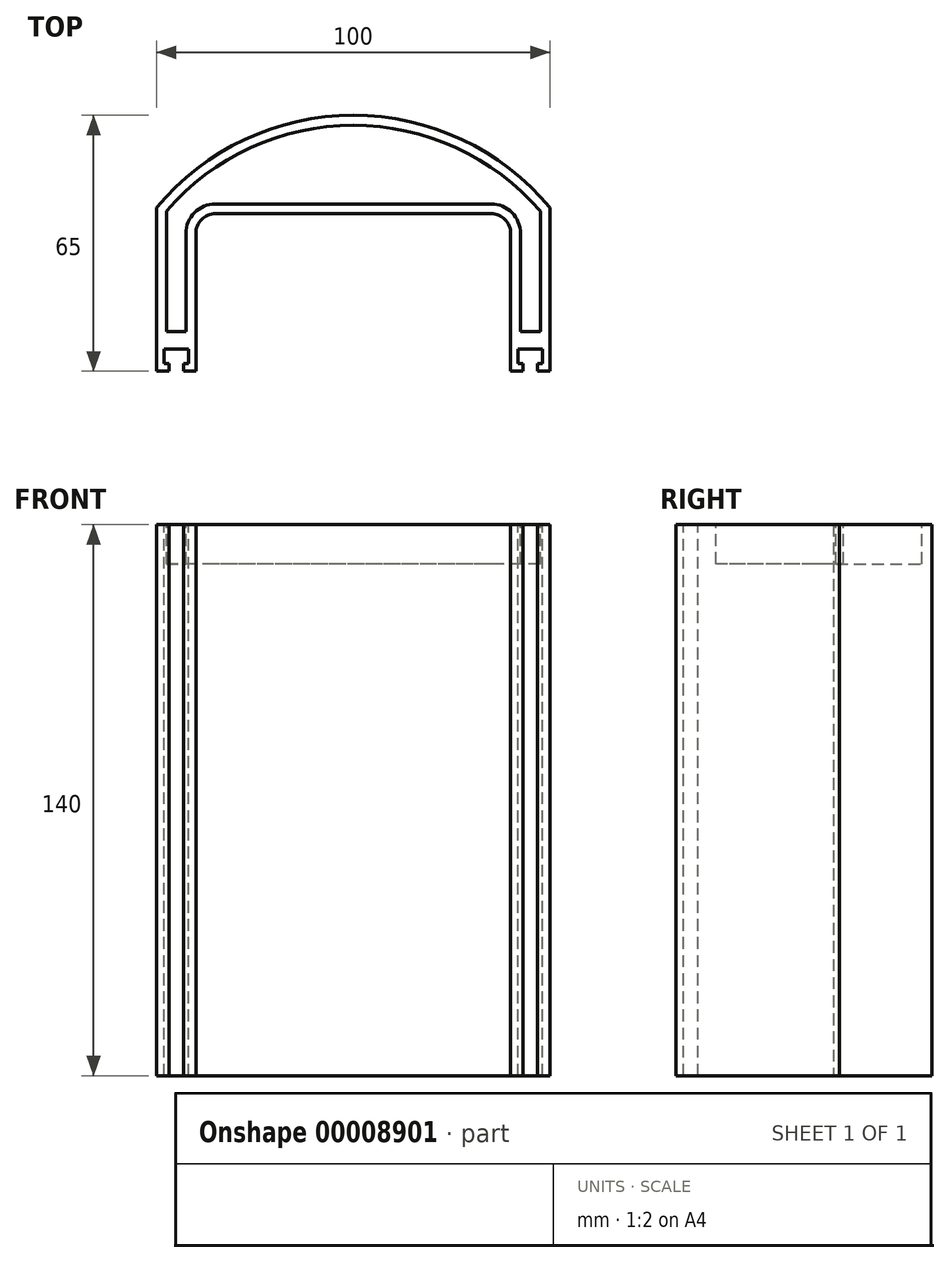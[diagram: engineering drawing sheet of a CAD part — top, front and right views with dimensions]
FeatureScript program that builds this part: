
annotation { "Feature Type Name" : "Feature", "Feature Type Description" : "" }
export const myFeature = defineFeature(function(context is Context, id is Id, definition is map)
    precondition{}
    {
        {
            var Q0;
            Q0=qCreatedBy(makeId("Top.planeOp"),FACE);
            var sketch = newSketch(context, id + "F0", { "sketchPlane" : qUnion([Q0])});
            skLineSegment(sketch, "E0", {"start": v(0, 0) * mm, "end": v(-40, 0) * mm});
            skLineSegment(sketch, "E1", {"start": v(0, 0) * mm, "end": v(40, 0) * mm});
            skLineSegment(sketch, "E2", {"start": v(0, 35) * mm, "end": v(0, 0) * mm});
            skLineSegment(sketch, "E3", {"start": v(-40, 0) * mm, "end": v(-43.59, 0) * mm});
            skLineSegment(sketch, "E4", {"start": v(40, 0) * mm, "end": v(43.59, 0) * mm});
            skLineSegment(sketch, "E5", {"start": v(-43.59, 0) * mm, "end": v(-50, 0) * mm});
            skLineSegment(sketch, "E6", {"start": v(43.59, 0) * mm, "end": v(50, 0) * mm});
            skCircle(sketch, "E7.0", {"center": v(0, 0) * mm, "radius": 65 * mm});
            skLineSegment(sketch, "E8.0", {"start": v(40, 35) * mm, "end": v(40, 0) * mm});
            skLineSegment(sketch, "E9.0", {"start": v(-40, 35) * mm, "end": v(-40, 0) * mm});
            skLineSegment(sketch, "E10.0", {"start": v(0, 40) * mm, "end": v(-35, 40) * mm});
            skLineSegment(sketch, "E10.1", {"start": v(0, 40) * mm, "end": v(35, 40) * mm});
            skPoint(sketch, "E11.visualSharp", {"position": v(-40, 40) * mm});
            skArc(sketch, "E11.filletArc", {"start": v(-35, 40) * mm, "mid": v(-38.54, 38.54) * mm, "end": v(-40, 35) * mm});
            skPoint(sketch, "E12.visualSharp", {"position": v(40, 40) * mm});
            skArc(sketch, "E12.filletArc", {"start": v(40, 35) * mm, "mid": v(38.54, 38.54) * mm, "end": v(35, 40) * mm});
            skLineSegment(sketch, "E13.0", {"start": v(-50, 41.53) * mm, "end": v(-50, 0) * mm});
            skLineSegment(sketch, "E14.0", {"start": v(50, 41.53) * mm, "end": v(50, 0) * mm});
            skSolve(sketch);
        }
        {
            var Q0;
            Q0=makeQuery(id+"F0.imprint","IMPRINT",FACE,{"disambiguationData":[TD([[makeQuery(id+"F0.imprint","IMPRINT",EDGE,{"derivedFrom":sQuery(id+"F0.wireOp",EDGE,"E3")}),-1.0]])]});
            extrude(context, id + "F1", {"entities" : qUnion([Q0]), "depth" : 190 * mm});
        }
        {
            var Q0;
            Q0=makeQuery(id+"F1.opExtrude","CAP_FACE",FACE,{"disambiguationData":[OSD([sQuery(id+"F0.wireOp",EDGE,"E3"),sQuery(id+"F0.wireOp",EDGE,"E4"),sQuery(id+"F0.wireOp",EDGE,"E5"),sQuery(id+"F0.wireOp",EDGE,"E6"),sQuery(id+"F0.wireOp",EDGE,"E7.0"),sQuery(id+"F0.wireOp",EDGE,"E8.0"),sQuery(id+"F0.wireOp",EDGE,"E9.0"),sQuery(id+"F0.wireOp",EDGE,"E10.0"),sQuery(id+"F0.wireOp",EDGE,"E10.1"),sQuery(id+"F0.wireOp",EDGE,"E11.filletArc"),sQuery(id+"F0.wireOp",EDGE,"E12.filletArc"),sQuery(id+"F0.wireOp",EDGE,"E13.0"),sQuery(id+"F0.wireOp",EDGE,"E14.0")])],"isStart":false});
            var sketch = newSketch(context, id + "F2", { "sketchPlane" : qUnion([Q0])});
            skLineSegment(sketch, "E15.0", {"start": v(35, 32.9) * mm, "end": v(35, 0) * mm});
            skLineSegment(sketch, "E16", {"start": v(-50, 0) * mm, "end": v(-50, 5) * mm});
            skLineSegment(sketch, "E17.0", {"start": v(-43.75, 0) * mm, "end": v(-43.75, 2.5) * mm, "construction": true});
            skLineSegment(sketch, "E18.0", {"start": v(-46.25, 0) * mm, "end": v(-46.25, 2.5) * mm, "construction": true});
            skLineSegment(sketch, "E19.0", {"start": v(-47.5, 2.5) * mm, "end": v(-47.5, 5) * mm, "construction": true});
            skLineSegment(sketch, "E20.0", {"start": v(-42.5, 2.5) * mm, "end": v(-42.5, 5) * mm, "construction": true});
            skLineSegment(sketch, "E21", {"start": v(-47.5, 5) * mm, "end": v(-42.5, 5) * mm, "construction": true});
            skLineSegment(sketch, "E22.0", {"start": v(-47.5, 2.5) * mm, "end": v(-46.25, 2.5) * mm, "construction": true});
            skLineSegment(sketch, "E23.trimOffspring", {"start": v(-43.75, 2.5) * mm, "end": v(-42.5, 2.5) * mm, "construction": true});
            skLineSegment(sketch, "E24.0", {"start": v(-48.1, 1.9) * mm, "end": v(-48.1, 5.6) * mm});
            skLineSegment(sketch, "E25.0", {"start": v(-48.1, 5.6) * mm, "end": v(-41.9, 5.6) * mm});
            skLineSegment(sketch, "E26.0", {"start": v(-41.9, 1.9) * mm, "end": v(-41.9, 5.6) * mm});
            skLineSegment(sketch, "E27.0", {"start": v(-48.1, 1.9) * mm, "end": v(-46.85, 1.9) * mm});
            skLineSegment(sketch, "E28.0", {"start": v(-43.15, 1.9) * mm, "end": v(-41.9, 1.9) * mm});
            skLineSegment(sketch, "E29.0", {"start": v(-46.85, 0) * mm, "end": v(-46.85, 1.9) * mm});
            skLineSegment(sketch, "E30.0", {"start": v(-43.15, 0) * mm, "end": v(-43.15, 1.9) * mm});
            skLineSegment(sketch, "E31", {"start": v(50, 0) * mm, "end": v(50, 5) * mm});
            skLineSegment(sketch, "E32.0", {"start": v(46.25, 0) * mm, "end": v(46.25, 2.5) * mm, "construction": true});
            skLineSegment(sketch, "E33.0", {"start": v(47.5, 2.5) * mm, "end": v(47.5, 5) * mm, "construction": true});
            skLineSegment(sketch, "E34.0", {"start": v(43.75, 0) * mm, "end": v(43.75, 2.5) * mm, "construction": true});
            skLineSegment(sketch, "E35.0", {"start": v(42.5, 2.5) * mm, "end": v(42.5, 5) * mm, "construction": true});
            skLineSegment(sketch, "E36", {"start": v(47.5, 5) * mm, "end": v(42.5, 5) * mm, "construction": true});
            skLineSegment(sketch, "E37.0", {"start": v(47.5, 2.5) * mm, "end": v(46.25, 2.5) * mm, "construction": true});
            skLineSegment(sketch, "E38.trimOffspring", {"start": v(43.75, 2.5) * mm, "end": v(42.5, 2.5) * mm, "construction": true});
            skLineSegment(sketch, "E39.0", {"start": v(48.1, 5.6) * mm, "end": v(41.9, 5.6) * mm});
            skLineSegment(sketch, "E40.0", {"start": v(48.1, 1.9) * mm, "end": v(48.1, 5.6) * mm});
            skLineSegment(sketch, "E41.0", {"start": v(41.9, 1.9) * mm, "end": v(41.9, 5.6) * mm});
            skLineSegment(sketch, "E42.0", {"start": v(43.15, 0) * mm, "end": v(43.15, 1.9) * mm});
            skLineSegment(sketch, "E43.0", {"start": v(46.85, 0) * mm, "end": v(46.85, 1.9) * mm});
            skLineSegment(sketch, "E44.0", {"start": v(48.1, 1.9) * mm, "end": v(46.85, 1.9) * mm});
            skLineSegment(sketch, "E45.0", {"start": v(43.15, 1.9) * mm, "end": v(41.9, 1.9) * mm});
            skSolve(sketch);
        }
        {
            var Q0;
            Q0=makeQuery(id+"F2.imprint","IMPRINT",FACE,{"disambiguationData":[TD([[makeQuery(id+"F2.imprint","IMPRINT",EDGE,{"derivedFrom":sQuery(id+"F2.wireOp",EDGE,"E39.0")}),1.0]])]});
            var Q1;
            Q1=makeQuery(id+"F2.imprint","IMPRINT",FACE,{"disambiguationData":[TD([[makeQuery(id+"F2.imprint","IMPRINT",EDGE,{"derivedFrom":sQuery(id+"F2.wireOp",EDGE,"E24.0")}),-1.0]])]});
            extrude(context, id + "F3", {"entities" : qUnion([Q0, Q1]), "operationType" : NewBodyOperationType.REMOVE, "oppositeDirection" : true, "depth" : 190 * mm});
        }
        {
            var Q0;
            Q0=makeQuery(id+"F1.opExtrude","CAP_FACE",FACE,{"disambiguationData":[OSD([sQuery(id+"F0.wireOp",EDGE,"E3"),sQuery(id+"F0.wireOp",EDGE,"E4"),sQuery(id+"F0.wireOp",EDGE,"E5"),sQuery(id+"F0.wireOp",EDGE,"E6"),sQuery(id+"F0.wireOp",EDGE,"E7.0"),sQuery(id+"F0.wireOp",EDGE,"E8.0"),sQuery(id+"F0.wireOp",EDGE,"E9.0"),sQuery(id+"F0.wireOp",EDGE,"E10.0"),sQuery(id+"F0.wireOp",EDGE,"E10.1"),sQuery(id+"F0.wireOp",EDGE,"E11.filletArc"),sQuery(id+"F0.wireOp",EDGE,"E12.filletArc"),sQuery(id+"F0.wireOp",EDGE,"E13.0"),sQuery(id+"F0.wireOp",EDGE,"E14.0")])],"isStart":false});
            extrude(context, id + "F4", {"entities" : qUnion([Q0]), "operationType" : NewBodyOperationType.REMOVE, "oppositeDirection" : true, "depth" : 50 * mm});
        }
        {
            var Q0;
            Q0=makeQuery(id+"F4.boolean.opBoolean","COPY",FACE,{"derivedFrom":makeQuery(id+"F4.opExtrude","CAP_FACE",FACE,{"disambiguationData":[OSD([sQuery(id+"F0.wireOp",EDGE,"E3"),sQuery(id+"F0.wireOp",EDGE,"E4"),sQuery(id+"F0.wireOp",EDGE,"E5"),sQuery(id+"F0.wireOp",EDGE,"E6"),sQuery(id+"F0.wireOp",EDGE,"E7.0"),sQuery(id+"F0.wireOp",EDGE,"E8.0"),sQuery(id+"F0.wireOp",EDGE,"E9.0"),sQuery(id+"F0.wireOp",EDGE,"E10.0"),sQuery(id+"F0.wireOp",EDGE,"E10.1"),sQuery(id+"F0.wireOp",EDGE,"E11.filletArc"),sQuery(id+"F0.wireOp",EDGE,"E12.filletArc"),sQuery(id+"F0.wireOp",EDGE,"E13.0"),sQuery(id+"F0.wireOp",EDGE,"E14.0")])],"isStart":false})});
            var sketch = newSketch(context, id + "F5", { "sketchPlane" : qUnion([Q0])});
            skLineSegment(sketch, "E46.0", {"start": v(-48.1, 10.6) * mm, "end": v(-41.9, 10.6) * mm, "construction": true});
            skLineSegment(sketch, "E47.0", {"start": v(48.1, 10.6) * mm, "end": v(41.9, 10.6) * mm, "construction": true});
            skLineSegment(sketch, "E48.0", {"start": v(-47.5, 40.62) * mm, "end": v(-47.5, 0) * mm});
            skArc(sketch, "E48.1", {"start": v(47.5, 40.62) * mm, "mid": v(0, 62.5) * mm, "end": v(-47.5, 40.62) * mm});
            skLineSegment(sketch, "E48.2", {"start": v(47.5, 40.62) * mm, "end": v(47.5, 0) * mm});
            skLineSegment(sketch, "E49.0", {"start": v(-42.5, 35) * mm, "end": v(-42.5, 0) * mm});
            skArc(sketch, "E49.1", {"start": v(-35, 42.5) * mm, "mid": v(-40.3, 40.3) * mm, "end": v(-42.5, 35) * mm});
            skLineSegment(sketch, "E49.2", {"start": v(35, 42.5) * mm, "end": v(-35, 42.5) * mm});
            skArc(sketch, "E49.3", {"start": v(42.5, 35) * mm, "mid": v(40.3, 40.3) * mm, "end": v(35, 42.5) * mm});
            skLineSegment(sketch, "E49.4", {"start": v(42.5, 35) * mm, "end": v(42.5, 0) * mm});
            skLineSegment(sketch, "E50.0", {"start": v(-48.1, 10.1) * mm, "end": v(-41.9, 10.1) * mm});
            skLineSegment(sketch, "E51.0", {"start": v(48.1, 10.1) * mm, "end": v(41.9, 10.1) * mm});
            skSolve(sketch);
        }
        {
            var Q0;
            {var subQ10=sQuery(id+"F5.wireOp",EDGE,"E48.1");Q0=makeQuery(id+"F5.imprint","IMPRINT",FACE,{"disambiguationData":[TD([[makeQuery(id+"F5.imprint","IMPRINT",EDGE,{"derivedFrom":subQ10}),1.0]])]});}
            extrude(context, id + "F6", {"entities" : qUnion([Q0]), "operationType" : NewBodyOperationType.REMOVE, "oppositeDirection" : true, "depth" : 10 * mm});
        }
    });
